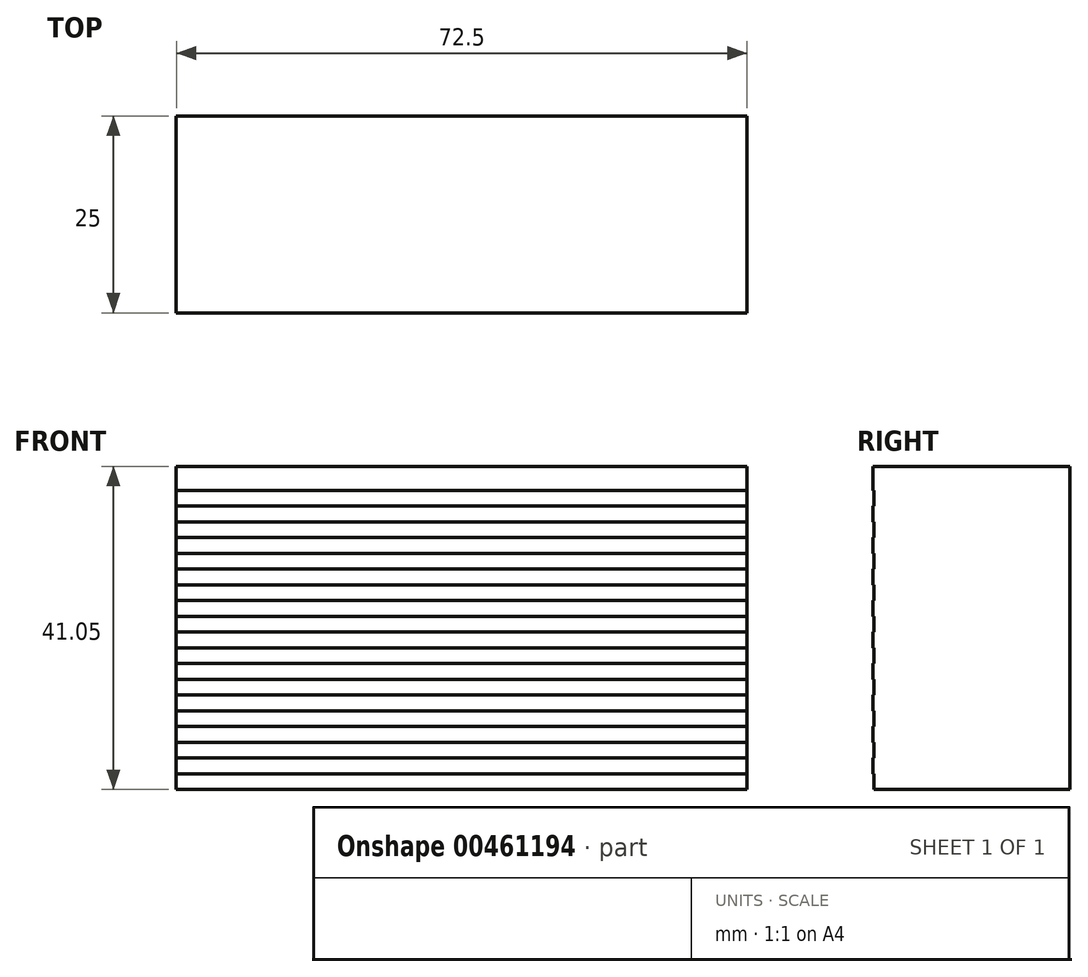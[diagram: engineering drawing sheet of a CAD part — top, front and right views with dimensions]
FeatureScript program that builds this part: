
annotation { "Feature Type Name" : "Feature", "Feature Type Description" : "" }
export const myFeature = defineFeature(function(context is Context, id is Id, definition is map)
    precondition{}
    {
        {
            var Q0;
            Q0=qCreatedBy(makeId("Front.planeOp"),FACE);
            var sketch = newSketch(context, id + "F0", { "sketchPlane" : qUnion([Q0])});
            skLineSegment(sketch, "E0.bottom", {"start": v(-26, 19.84) * mm, "end": v(46.51, 19.84) * mm});
            skLineSegment(sketch, "E0.top", {"start": v(-26, -21.2) * mm, "end": v(46.51, -21.2) * mm});
            skLineSegment(sketch, "E0.left", {"start": v(-26, 19.84) * mm, "end": v(-26, -21.2) * mm});
            skLineSegment(sketch, "E0.right", {"start": v(46.51, 19.84) * mm, "end": v(46.51, -21.2) * mm});
            skSolve(sketch);
        }
        {
            var Q0;
            Q0 = qSketchRegion(id + "F0", true);
            extrude(context, id + "F1", {"entities" : qUnion([Q0]), "depth" : 25 * mm});
        }
        {
            var Q0;
            Q0=makeQuery(id+"F1.opExtrude","CAP_FACE",FACE,{"disambiguationData":[OSD([sQuery(id+"F0.wireOp",EDGE,"E0.bottom"),sQuery(id+"F0.wireOp",EDGE,"E0.top"),sQuery(id+"F0.wireOp",EDGE,"E0.left"),sQuery(id+"F0.wireOp",EDGE,"E0.right")])],"isStart":false});
            var sketch = newSketch(context, id + "F2", { "sketchPlane" : qUnion([Q0])});
            skLineSegment(sketch, "E1.bottom", {"start": v(-26, -21.2) * mm, "end": v(46.51, -21.2) * mm});
            skLineSegment(sketch, "E1.top", {"start": v(-26, -19.2) * mm, "end": v(46.51, -19.2) * mm});
            skLineSegment(sketch, "E1.left", {"start": v(-26, -21.2) * mm, "end": v(-26, -19.2) * mm});
            skLineSegment(sketch, "E1.right", {"start": v(46.51, -21.2) * mm, "end": v(46.51, -19.2) * mm});
            skLineSegment(sketch, "E2.0.1.0", {"start": v(-26, -17.2) * mm, "end": v(46.51, -17.2) * mm});
            skLineSegment(sketch, "E2.0.1.1", {"start": v(-26, -15.2) * mm, "end": v(46.51, -15.2) * mm});
            skLineSegment(sketch, "E2.0.1.2", {"start": v(-26, -17.2) * mm, "end": v(-26, -15.2) * mm});
            skLineSegment(sketch, "E2.0.1.3", {"start": v(46.51, -17.2) * mm, "end": v(46.51, -15.2) * mm});
            skLineSegment(sketch, "E2.0.2.0", {"start": v(-26, -13.2) * mm, "end": v(46.51, -13.2) * mm});
            skLineSegment(sketch, "E2.0.2.1", {"start": v(-26, -11.2) * mm, "end": v(46.51, -11.2) * mm});
            skLineSegment(sketch, "E2.0.2.2", {"start": v(-26, -13.2) * mm, "end": v(-26, -11.2) * mm});
            skLineSegment(sketch, "E2.0.2.3", {"start": v(46.51, -13.2) * mm, "end": v(46.51, -11.2) * mm});
            skLineSegment(sketch, "E2.0.3.0", {"start": v(-26, -9.2) * mm, "end": v(46.51, -9.2) * mm});
            skLineSegment(sketch, "E2.0.3.1", {"start": v(-26, -7.2) * mm, "end": v(46.51, -7.2) * mm});
            skLineSegment(sketch, "E2.0.3.2", {"start": v(-26, -9.2) * mm, "end": v(-26, -7.2) * mm});
            skLineSegment(sketch, "E2.0.3.3", {"start": v(46.51, -9.2) * mm, "end": v(46.51, -7.2) * mm});
            skLineSegment(sketch, "E2.0.4.0", {"start": v(-26, -5.2) * mm, "end": v(46.51, -5.2) * mm});
            skLineSegment(sketch, "E2.0.4.1", {"start": v(-26, -3.2) * mm, "end": v(46.51, -3.2) * mm});
            skLineSegment(sketch, "E2.0.4.2", {"start": v(-26, -5.2) * mm, "end": v(-26, -3.2) * mm});
            skLineSegment(sketch, "E2.0.4.3", {"start": v(46.51, -5.2) * mm, "end": v(46.51, -3.2) * mm});
            skLineSegment(sketch, "E2.0.5.0", {"start": v(-26, -1.2) * mm, "end": v(46.51, -1.2) * mm});
            skLineSegment(sketch, "E2.0.5.1", {"start": v(-26, 0.8) * mm, "end": v(46.51, 0.8) * mm});
            skLineSegment(sketch, "E2.0.5.2", {"start": v(-26, -1.2) * mm, "end": v(-26, 0.8) * mm});
            skLineSegment(sketch, "E2.0.5.3", {"start": v(46.51, -1.2) * mm, "end": v(46.51, 0.8) * mm});
            skLineSegment(sketch, "E2.0.6.0", {"start": v(-26, 2.8) * mm, "end": v(46.51, 2.8) * mm});
            skLineSegment(sketch, "E2.0.6.1", {"start": v(-26, 4.8) * mm, "end": v(46.51, 4.8) * mm});
            skLineSegment(sketch, "E2.0.6.2", {"start": v(-26, 2.8) * mm, "end": v(-26, 4.8) * mm});
            skLineSegment(sketch, "E2.0.6.3", {"start": v(46.51, 2.8) * mm, "end": v(46.51, 4.8) * mm});
            skLineSegment(sketch, "E2.0.7.0", {"start": v(-26, 6.8) * mm, "end": v(46.51, 6.8) * mm});
            skLineSegment(sketch, "E2.0.7.1", {"start": v(-26, 8.8) * mm, "end": v(46.51, 8.8) * mm});
            skLineSegment(sketch, "E2.0.7.2", {"start": v(-26, 6.8) * mm, "end": v(-26, 8.8) * mm});
            skLineSegment(sketch, "E2.0.7.3", {"start": v(46.51, 6.8) * mm, "end": v(46.51, 8.8) * mm});
            skLineSegment(sketch, "E2.0.8.0", {"start": v(-26, 10.8) * mm, "end": v(46.51, 10.8) * mm});
            skLineSegment(sketch, "E2.0.8.1", {"start": v(-26, 12.8) * mm, "end": v(46.51, 12.8) * mm});
            skLineSegment(sketch, "E2.0.8.2", {"start": v(-26, 10.8) * mm, "end": v(-26, 12.8) * mm});
            skLineSegment(sketch, "E2.0.8.3", {"start": v(46.51, 10.8) * mm, "end": v(46.51, 12.8) * mm});
            skLineSegment(sketch, "E2.0.9.0", {"start": v(-26, 14.8) * mm, "end": v(46.51, 14.8) * mm});
            skLineSegment(sketch, "E2.0.9.1", {"start": v(-26, 16.8) * mm, "end": v(46.51, 16.8) * mm});
            skLineSegment(sketch, "E2.0.9.2", {"start": v(-26, 14.8) * mm, "end": v(-26, 16.8) * mm});
            skLineSegment(sketch, "E2.0.9.3", {"start": v(46.51, 14.8) * mm, "end": v(46.51, 16.8) * mm});
            skLineSegment(sketch, "E2.direction1", {"start": v(-26, -21.2) * mm, "end": v(-1, -21.2) * mm, "construction": true});
            skLineSegment(sketch, "E2.direction2", {"start": v(-26, -21.2) * mm, "end": v(-26, -17.2) * mm, "construction": true});
            skSolve(sketch);
        }
        {
            var Q0;
            Q0 = qSketchRegion(id + "F2", true);
            extrude(context, id + "F3", {"entities" : qUnion([Q0]), "operationType" : NewBodyOperationType.REMOVE, "oppositeDirection" : true, "depth" : 0.1 * mm});
        }
    });
